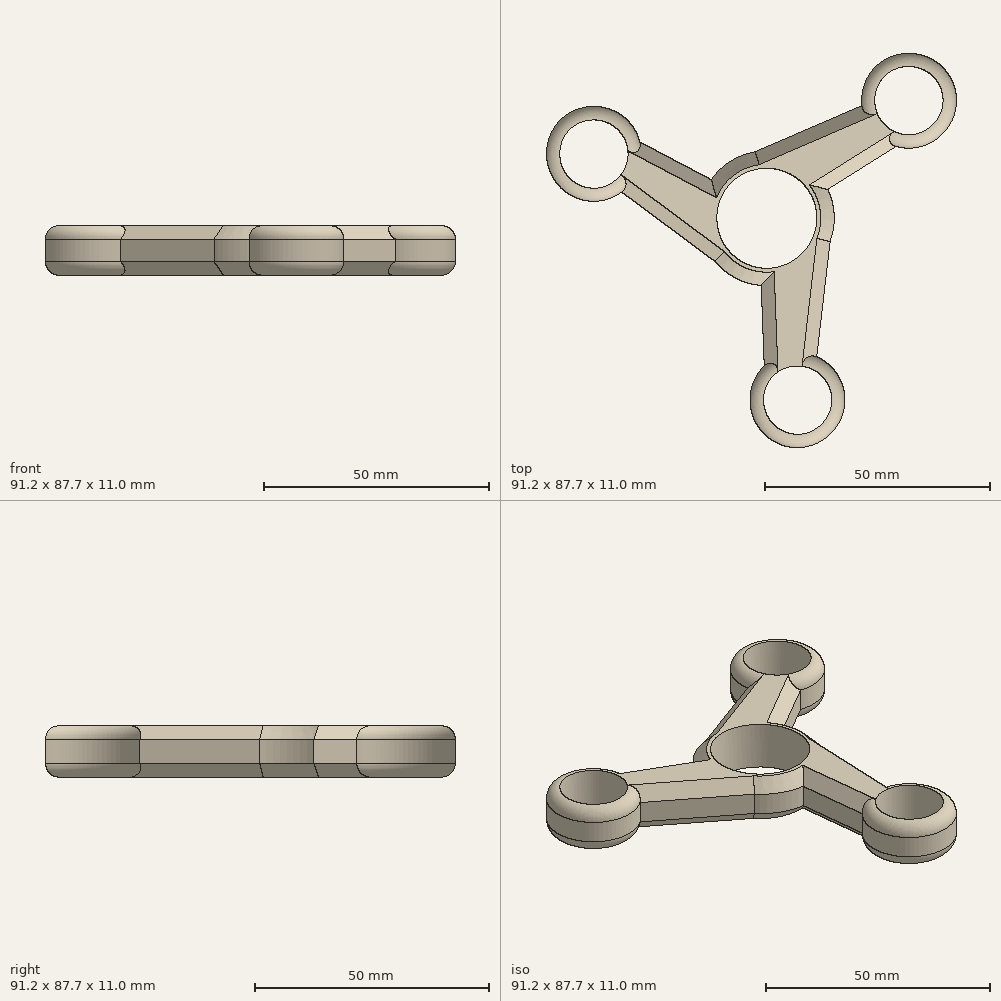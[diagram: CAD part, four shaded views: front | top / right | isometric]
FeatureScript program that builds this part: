
annotation { "Feature Type Name" : "Feature", "Feature Type Description" : "" }
export const myFeature = defineFeature(function(context is Context, id is Id, definition is map)
    precondition{}
    {
        {
            var Q0;
            Q0=qCreatedBy(makeId("Top.planeOp"),FACE);
            var sketch = newSketch(context, id + "F0", { "sketchPlane" : qUnion([Q0])});
            skCircle(sketch, "E0", {"center": v(0, 0) * mm, "radius": 11.12 * mm});
            skCircle(sketch, "E1", {"center": v(0, 0) * mm, "radius": 15 * mm});
            skPoint(sketch, "E2.center", {"position": v(-0.19, 0.15) * mm});
            skPoint(sketch, "E3.center", {"position": v(-0.7, 0.02) * mm});
            skPoint(sketch, "E4.center", {"position": v(-0.13, -1.49) * mm});
            skLineSegment(sketch, "E5.1.0", {"start": v(-11.52, -9.6) * mm, "end": v(-32.22, 5.8) * mm});
            skCircle(sketch, "E6.cCircle", {"center": v(31.62, 26.13) * mm, "radius": 4.77 * mm, "construction": true});
            skLineSegment(sketch, "E6.0", {"start": v(34.37, 21.36) * mm, "end": v(28.86, 21.36) * mm});
            skLineSegment(sketch, "E6.1", {"start": v(28.86, 21.36) * mm, "end": v(26.1, 26.13) * mm});
            skLineSegment(sketch, "E6.2", {"start": v(26.1, 26.13) * mm, "end": v(28.86, 30.9) * mm});
            skLineSegment(sketch, "E6.3", {"start": v(28.86, 30.9) * mm, "end": v(34.37, 30.9) * mm});
            skLineSegment(sketch, "E6.4", {"start": v(34.37, 30.9) * mm, "end": v(37.13, 26.13) * mm});
            skLineSegment(sketch, "E6.5", {"start": v(37.13, 26.13) * mm, "end": v(34.37, 21.36) * mm});
            skPoint(sketch, "E6.0.midPoint", {"position": v(31.62, 21.36) * mm});
            skLineSegment(sketch, "E7.1.0", {"start": v(-35.69, 9.55) * mm, "end": v(-41.2, 9.55) * mm});
            skCircle(sketch, "E7.1.1", {"center": v(-38.44, 14.32) * mm, "radius": 4.77 * mm, "construction": true});
            skLineSegment(sketch, "E7.1.2", {"start": v(-43.95, 14.32) * mm, "end": v(-41.2, 19.1) * mm});
            skLineSegment(sketch, "E7.1.3", {"start": v(-35.69, 19.1) * mm, "end": v(-32.93, 14.32) * mm});
            skLineSegment(sketch, "E7.1.4", {"start": v(-41.2, 19.1) * mm, "end": v(-35.69, 19.1) * mm});
            skLineSegment(sketch, "E7.1.5", {"start": v(-32.93, 14.32) * mm, "end": v(-35.69, 9.55) * mm});
            skPoint(sketch, "E7.1.6", {"position": v(-34.3, 16.7) * mm});
            skLineSegment(sketch, "E7.1.7", {"start": v(-41.2, 9.55) * mm, "end": v(-43.95, 14.32) * mm});
            skLineSegment(sketch, "E7.2.0", {"start": v(9.57, -35.67) * mm, "end": v(12.33, -40.45) * mm});
            skCircle(sketch, "E7.2.1", {"center": v(6.81, -40.45) * mm, "radius": 4.77 * mm, "construction": true});
            skLineSegment(sketch, "E7.2.2", {"start": v(9.57, -45.22) * mm, "end": v(4.06, -45.22) * mm});
            skLineSegment(sketch, "E7.2.3", {"start": v(1.3, -40.45) * mm, "end": v(4.06, -35.67) * mm});
            skLineSegment(sketch, "E7.2.4", {"start": v(4.06, -45.22) * mm, "end": v(1.3, -40.45) * mm});
            skLineSegment(sketch, "E7.2.5", {"start": v(4.06, -35.67) * mm, "end": v(9.57, -35.67) * mm});
            skPoint(sketch, "E7.2.6", {"position": v(2.68, -38.06) * mm});
            skLineSegment(sketch, "E7.2.7", {"start": v(12.33, -40.45) * mm, "end": v(9.57, -45.22) * mm});
            skCircle(sketch, "E8", {"center": v(-38.44, 14.32) * mm, "radius": 10.55 * mm});
            skLineSegment(sketch, "E9", {"start": v(-12.32, 8.56) * mm, "end": v(-28.22, 16.96) * mm});
            skCircle(sketch, "E10.1.0", {"center": v(6.82, -40.45) * mm, "radius": 10.55 * mm});
            skCircle(sketch, "E10.2.0", {"center": v(31.62, 26.13) * mm, "radius": 10.55 * mm});
            skLineSegment(sketch, "E11.1.0", {"start": v(-1.25, -14.95) * mm, "end": v(-0.58, -32.92) * mm});
            skLineSegment(sketch, "E11.2.0", {"start": v(13.57, 6.39) * mm, "end": v(28.8, 15.96) * mm});
            skLineSegment(sketch, "E12.1.0", {"start": v(14.08, -5.18) * mm, "end": v(11.1, -30.8) * mm});
            skLineSegment(sketch, "E12.2.0", {"start": v(-2.56, 14.78) * mm, "end": v(21.13, 25) * mm});
            skSolve(sketch);
        }
        {
            var Q0;
            {var subQ0=sQuery(id+"F0.wireOp",EDGE,"E11.1.0");Q0=makeQuery(id+"F0.imprint","IMPRINT",FACE,{"disambiguationData":[TD([[makeQuery(id+"F0.imprint","IMPRINT",EDGE,{"derivedFrom":subQ0}),1.0]])]});}
            var Q1;
            Q1=makeQuery(id+"F0.imprint","IMPRINT",FACE,{"disambiguationData":[TD([[makeQuery(id+"F0.imprint","IMPRINT",EDGE,{"derivedFrom":sQuery(id+"F0.wireOp",EDGE,"E7.2.0")}),1.0]])]});
            var Q2;
            Q2=makeQuery(id+"F0.imprint","IMPRINT",FACE,{"disambiguationData":[TD([[makeQuery(id+"F0.imprint","IMPRINT",EDGE,{"derivedFrom":sQuery(id+"F0.wireOp",EDGE,"E0")}),-1.0]])]});
            var Q3;
            {var subQ0=sQuery(id+"F0.wireOp",EDGE,"E5.1.0");Q3=makeQuery(id+"F0.imprint","IMPRINT",FACE,{"disambiguationData":[TD([[makeQuery(id+"F0.imprint","IMPRINT",EDGE,{"derivedFrom":subQ0}),-1.0]])]});}
            var Q4;
            Q4=makeQuery(id+"F0.imprint","IMPRINT",FACE,{"disambiguationData":[TD([[makeQuery(id+"F0.imprint","IMPRINT",EDGE,{"derivedFrom":sQuery(id+"F0.wireOp",EDGE,"E0")}),1.0]])]});
            var Q5;
            {var subQ0=sQuery(id+"F0.wireOp",EDGE,"E11.2.0");Q5=makeQuery(id+"F0.imprint","IMPRINT",FACE,{"disambiguationData":[TD([[makeQuery(id+"F0.imprint","IMPRINT",EDGE,{"derivedFrom":subQ0}),1.0]])]});}
            var Q6;
            Q6=makeQuery(id+"F0.imprint","IMPRINT",FACE,{"disambiguationData":[TD([[makeQuery(id+"F0.imprint","IMPRINT",EDGE,{"derivedFrom":sQuery(id+"F0.wireOp",EDGE,"E6.0")}),1.0]])]});
            var Q7;
            Q7=makeQuery(id+"F0.imprint","IMPRINT",FACE,{"disambiguationData":[TD([[makeQuery(id+"F0.imprint","IMPRINT",EDGE,{"derivedFrom":sQuery(id+"F0.wireOp",EDGE,"E7.2.0")}),-1.0]])]});
            var Q8;
            Q8=makeQuery(id+"F0.imprint","IMPRINT",FACE,{"disambiguationData":[TD([[makeQuery(id+"F0.imprint","IMPRINT",EDGE,{"derivedFrom":sQuery(id+"F0.wireOp",EDGE,"E7.1.0")}),1.0]])]});
            var Q9;
            Q9=makeQuery(id+"F0.imprint","IMPRINT",FACE,{"disambiguationData":[TD([[makeQuery(id+"F0.imprint","IMPRINT",EDGE,{"derivedFrom":sQuery(id+"F0.wireOp",EDGE,"E6.0")}),-1.0]])]});
            var Q10;
            Q10=makeQuery(id+"F0.imprint","IMPRINT",FACE,{"disambiguationData":[TD([[makeQuery(id+"F0.imprint","IMPRINT",EDGE,{"derivedFrom":sQuery(id+"F0.wireOp",EDGE,"E7.1.0")}),-1.0]])]});
            extrude(context, id + "F1", {"entities" : qUnion([Q0, Q1, Q2, Q3, Q4, Q5, Q6, Q7, Q8, Q9, Q10]), "depth" : 11 * mm, "offsetDistance" : 25 * mm});
        }
        {
            var Q0;
            Q0=makeQuery(id+"F1.opExtrude","CAP_EDGE",EDGE,{"disambiguationData":[OSD([sQuery(id+"F0.wireOp",EDGE,"E8")])],"isStart":false});
            var Q1;
            Q1=makeQuery(id+"F1.opExtrude","CAP_EDGE",EDGE,{"disambiguationData":[OSD([sQuery(id+"F0.wireOp",EDGE,"E10.2.0")])],"isStart":false});
            var Q2;
            Q2=makeQuery(id+"F1.opExtrude","CAP_EDGE",EDGE,{"disambiguationData":[OSD([sQuery(id+"F0.wireOp",EDGE,"E10.1.0")])],"isStart":false});
            var Q3;
            Q3=makeQuery(id+"F1.opExtrude","CAP_EDGE",EDGE,{"disambiguationData":[OSD([sQuery(id+"F0.wireOp",EDGE,"E10.2.0")])],"isStart":true});
            var Q4;
            Q4=makeQuery(id+"F1.opExtrude","CAP_EDGE",EDGE,{"disambiguationData":[OSD([sQuery(id+"F0.wireOp",EDGE,"E10.1.0")])],"isStart":true});
            var Q5;
            Q5=makeQuery(id+"F1.opExtrude","CAP_EDGE",EDGE,{"disambiguationData":[OSD([sQuery(id+"F0.wireOp",EDGE,"E8")])],"isStart":true});
            fillet(context, id + "F2", {"entities" : qUnion([Q0, Q1, Q2, Q3, Q4, Q5]), "radius" : 3 * mm, "tangentPropagation" : true, "allowEdgeOverflow" : false});
        }
        {
            var Q0;
            Q0=qCreatedBy(makeId("Top.planeOp"),FACE);
            var sketch = newSketch(context, id + "F3", { "sketchPlane" : qUnion([Q0])});
            skCircle(sketch, "E13", {"center": v(0, 0) * mm, "radius": 11.12 * mm});
            skSolve(sketch);
        }
        {
            var Q0;
            Q0=sQuery(id+"F3.wireOp",VERTEX,"E13.center");
            var Q1;
            Q1=makeQuery(id+"F1.opExtrude","SWEPT_BODY",BODY,{"disambiguationData":[OSD([sQuery(id+"F0.wireOp",EDGE,"E1"),sQuery(id+"F0.wireOp",EDGE,"E5.1.0"),sQuery(id+"F0.wireOp",EDGE,"E8"),sQuery(id+"F0.wireOp",EDGE,"E9"),sQuery(id+"F0.wireOp",EDGE,"E10.1.0"),sQuery(id+"F0.wireOp",EDGE,"E10.2.0"),sQuery(id+"F0.wireOp",EDGE,"E11.1.0"),sQuery(id+"F0.wireOp",EDGE,"E11.2.0"),sQuery(id+"F0.wireOp",EDGE,"E12.1.0"),sQuery(id+"F0.wireOp",EDGE,"E12.2.0")])]});
            hole(context, id + "F4", {"style" : HoleStyle.SIMPLE, "endStyle" : HoleEndStyle.THROUGH, "oppositeDirection" : true, "holeDiameter" : 22.25 * mm, "majorDiameter" : 5 * mm, "isTappedThrough" : true, "tappedDepth" : 12 * mm, "tapClearance" : 3, "locations" : qUnion([Q0]), "scope" : qUnion([Q1])});
        }
        {
            var Q0;
            Q0=qCreatedBy(makeId("Top.planeOp"),FACE);
            var sketch = newSketch(context, id + "F5", { "sketchPlane" : qUnion([Q0])});
            skCircle(sketch, "E14", {"center": v(31.59, 26.16) * mm, "radius": 5.5 * mm});
            skCircle(sketch, "E15.1.0", {"center": v(-38.45, 14.27) * mm, "radius": 5.5 * mm});
            skCircle(sketch, "E15.2.0", {"center": v(6.86, -40.44) * mm, "radius": 5.5 * mm});
            skPoint(sketch, "E15.center", {"position": v(0, 0) * mm});
            skSolve(sketch);
        }
        {
            var Q0;
            Q0=sQuery(id+"F5.wireOp",VERTEX,"E14.center");
            var Q1;
            Q1=sQuery(id+"F5.wireOp",VERTEX,"E15.2.0.center");
            var Q2;
            Q2=sQuery(id+"F5.wireOp",VERTEX,"E15.1.0.center");
            var Q3;
            Q3=makeQuery(id+"F1.opExtrude","SWEPT_BODY",BODY,{"disambiguationData":[OSD([sQuery(id+"F0.wireOp",EDGE,"E1"),sQuery(id+"F0.wireOp",EDGE,"E5.1.0"),sQuery(id+"F0.wireOp",EDGE,"E8"),sQuery(id+"F0.wireOp",EDGE,"E9"),sQuery(id+"F0.wireOp",EDGE,"E10.1.0"),sQuery(id+"F0.wireOp",EDGE,"E10.2.0"),sQuery(id+"F0.wireOp",EDGE,"E11.1.0"),sQuery(id+"F0.wireOp",EDGE,"E11.2.0"),sQuery(id+"F0.wireOp",EDGE,"E12.1.0"),sQuery(id+"F0.wireOp",EDGE,"E12.2.0")])]});
            hole(context, id + "F6", {"style" : HoleStyle.SIMPLE, "endStyle" : HoleEndStyle.THROUGH, "oppositeDirection" : true, "holeDiameter" : 15.2 * mm, "majorDiameter" : 5 * mm, "isTappedThrough" : true, "tappedDepth" : 12 * mm, "tapClearance" : 3, "locations" : qUnion([Q0, Q1, Q2]), "scope" : qUnion([Q3])});
        }
        {
            var Q0;
            {var subQ0=sQuery(id+"F0.wireOp",EDGE,"E1");Q0=makeQuery(id+"F1.opExtrude","CAP_EDGE",EDGE,{"disambiguationData":[OSD([subQ0]),TDD([makeQuery(id+"F0.imprint","IMPRINT",EDGE,{"disambiguationData":[TD([[makeQuery(id+"F0.imprint","INTERSECT",VERTEX,{"derivedFrom":[subQ0,sQuery(id+"F0.wireOp",EDGE,"E5.1.0")]}),-1.0]])],"derivedFrom":subQ0})])],"isStart":true});}
            var Q1;
            Q1=makeQuery(id+"F1.opExtrude","CAP_EDGE",EDGE,{"disambiguationData":[OSD([sQuery(id+"F0.wireOp",EDGE,"E5.1.0")])],"isStart":true});
            var Q2;
            Q2=makeQuery(id+"F1.opExtrude","CAP_EDGE",EDGE,{"disambiguationData":[OSD([sQuery(id+"F0.wireOp",EDGE,"E11.1.0")])],"isStart":true});
            var Q3;
            Q3=makeQuery(id+"F1.opExtrude","CAP_EDGE",EDGE,{"disambiguationData":[OSD([sQuery(id+"F0.wireOp",EDGE,"E12.1.0")])],"isStart":true});
            var Q4;
            {var subQ0=sQuery(id+"F0.wireOp",EDGE,"E1");Q4=makeQuery(id+"F1.opExtrude","CAP_EDGE",EDGE,{"disambiguationData":[OSD([subQ0]),TDD([makeQuery(id+"F0.imprint","IMPRINT",EDGE,{"disambiguationData":[TD([[makeQuery(id+"F0.imprint","INTERSECT",VERTEX,{"derivedFrom":[subQ0,sQuery(id+"F0.wireOp",EDGE,"E11.2.0")]}),1.0]])],"derivedFrom":subQ0})])],"isStart":true});}
            var Q5;
            Q5=makeQuery(id+"F1.opExtrude","CAP_EDGE",EDGE,{"disambiguationData":[OSD([sQuery(id+"F0.wireOp",EDGE,"E11.2.0")])],"isStart":true});
            var Q6;
            Q6=makeQuery(id+"F1.opExtrude","CAP_EDGE",EDGE,{"disambiguationData":[OSD([sQuery(id+"F0.wireOp",EDGE,"E12.2.0")])],"isStart":true});
            var Q7;
            {var subQ0=sQuery(id+"F0.wireOp",EDGE,"E1");Q7=makeQuery(id+"F1.opExtrude","CAP_EDGE",EDGE,{"disambiguationData":[OSD([subQ0]),TDD([makeQuery(id+"F0.imprint","IMPRINT",EDGE,{"disambiguationData":[TD([[makeQuery(id+"F0.imprint","INTERSECT",VERTEX,{"derivedFrom":[subQ0,sQuery(id+"F0.wireOp",EDGE,"E9")]}),1.0]])],"derivedFrom":subQ0})])],"isStart":true});}
            var Q8;
            Q8=makeQuery(id+"F1.opExtrude","CAP_EDGE",EDGE,{"disambiguationData":[OSD([sQuery(id+"F0.wireOp",EDGE,"E9")])],"isStart":true});
            var Q9;
            Q9=makeQuery(id+"F1.opExtrude","CAP_EDGE",EDGE,{"disambiguationData":[OSD([sQuery(id+"F0.wireOp",EDGE,"E12.2.0")])],"isStart":false});
            var Q10;
            Q10=makeQuery(id+"F1.opExtrude","CAP_EDGE",EDGE,{"disambiguationData":[OSD([sQuery(id+"F0.wireOp",EDGE,"E11.2.0")])],"isStart":false});
            var Q11;
            {var subQ0=sQuery(id+"F0.wireOp",EDGE,"E1");Q11=makeQuery(id+"F1.opExtrude","CAP_EDGE",EDGE,{"disambiguationData":[OSD([subQ0]),TDD([makeQuery(id+"F0.imprint","IMPRINT",EDGE,{"disambiguationData":[TD([[makeQuery(id+"F0.imprint","INTERSECT",VERTEX,{"derivedFrom":[subQ0,sQuery(id+"F0.wireOp",EDGE,"E9")]}),1.0]])],"derivedFrom":subQ0})])],"isStart":false});}
            var Q12;
            {var subQ0=sQuery(id+"F0.wireOp",EDGE,"E1");Q12=makeQuery(id+"F1.opExtrude","CAP_EDGE",EDGE,{"disambiguationData":[OSD([subQ0]),TDD([makeQuery(id+"F0.imprint","IMPRINT",EDGE,{"disambiguationData":[TD([[makeQuery(id+"F0.imprint","INTERSECT",VERTEX,{"derivedFrom":[subQ0,sQuery(id+"F0.wireOp",EDGE,"E11.2.0")]}),1.0]])],"derivedFrom":subQ0})])],"isStart":false});}
            var Q13;
            {var subQ0=sQuery(id+"F0.wireOp",EDGE,"E1");Q13=makeQuery(id+"F1.opExtrude","CAP_EDGE",EDGE,{"disambiguationData":[OSD([subQ0]),TDD([makeQuery(id+"F0.imprint","IMPRINT",EDGE,{"disambiguationData":[TD([[makeQuery(id+"F0.imprint","INTERSECT",VERTEX,{"derivedFrom":[subQ0,sQuery(id+"F0.wireOp",EDGE,"E5.1.0")]}),-1.0]])],"derivedFrom":subQ0})])],"isStart":false});}
            var Q14;
            Q14=makeQuery(id+"F1.opExtrude","CAP_EDGE",EDGE,{"disambiguationData":[OSD([sQuery(id+"F0.wireOp",EDGE,"E12.1.0")])],"isStart":false});
            var Q15;
            Q15=makeQuery(id+"F1.opExtrude","CAP_EDGE",EDGE,{"disambiguationData":[OSD([sQuery(id+"F0.wireOp",EDGE,"E11.1.0")])],"isStart":false});
            var Q16;
            Q16=makeQuery(id+"F1.opExtrude","CAP_EDGE",EDGE,{"disambiguationData":[OSD([sQuery(id+"F0.wireOp",EDGE,"E5.1.0")])],"isStart":false});
            var Q17;
            Q17=makeQuery(id+"F1.opExtrude","CAP_EDGE",EDGE,{"disambiguationData":[OSD([sQuery(id+"F0.wireOp",EDGE,"E9")])],"isStart":false});
            chamfer(context, id + "F7", {"entities" : qUnion([Q0, Q1, Q2, Q3, Q4, Q5, Q6, Q7, Q8, Q9, Q10, Q11, Q12, Q13, Q14, Q15, Q16, Q17]), "width" : 3 * mm, "tangentPropagation" : true});
        }
    });
